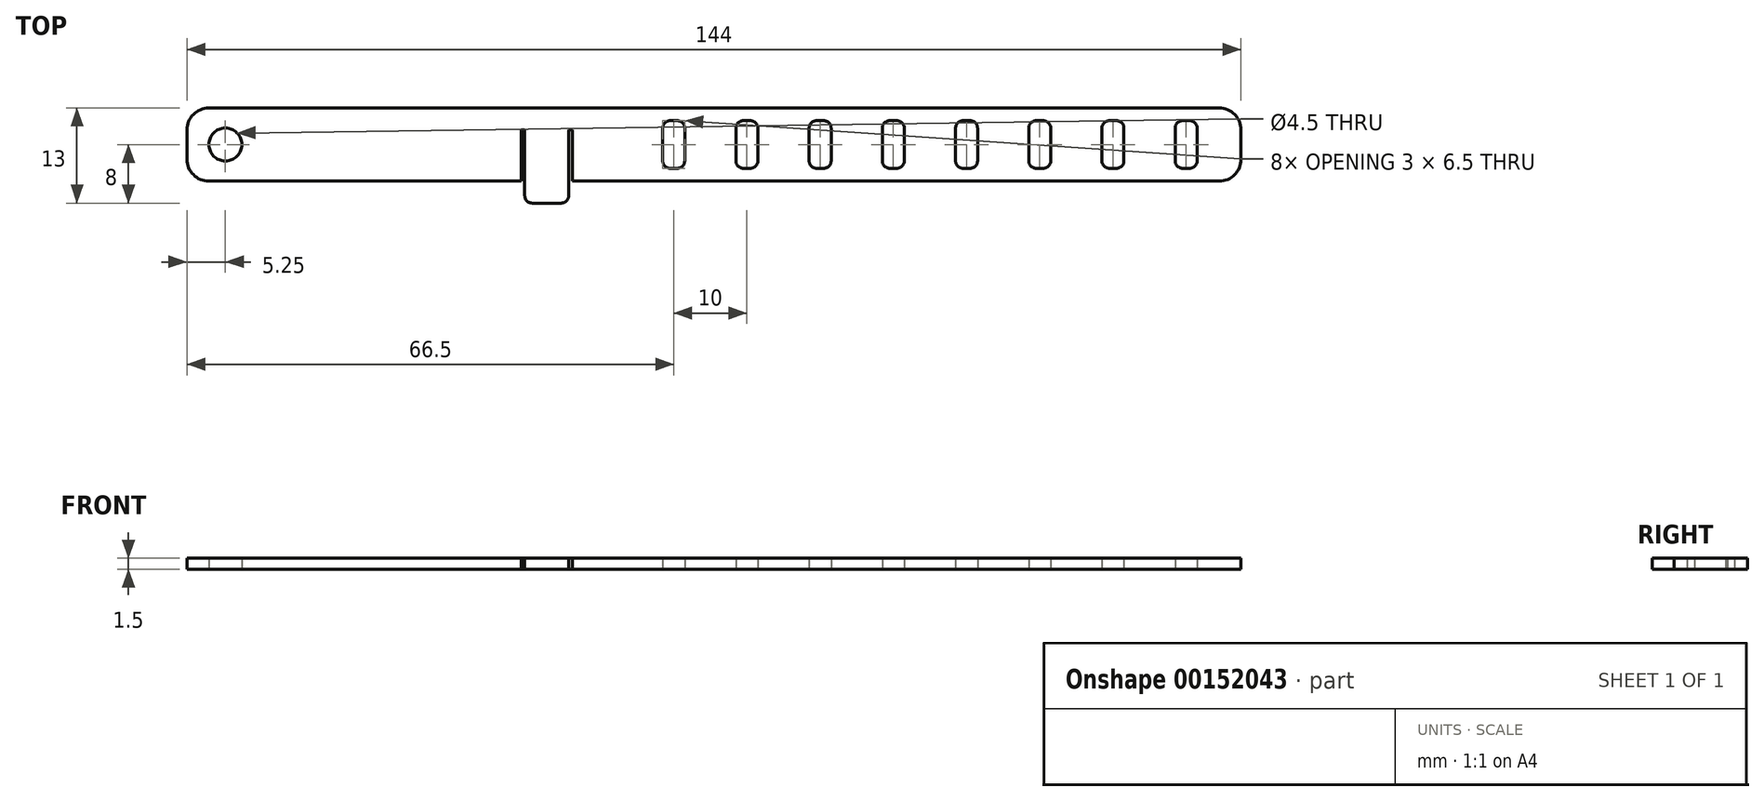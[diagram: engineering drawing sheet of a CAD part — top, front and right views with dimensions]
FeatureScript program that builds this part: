
annotation { "Feature Type Name" : "Feature", "Feature Type Description" : "" }
export const myFeature = defineFeature(function(context is Context, id is Id, definition is map)
    precondition{}
    {
        {
            var Q0;
            Q0=qCreatedBy(makeId("Top.planeOp"),FACE);
            var sketch = newSketch(context, id + "F0", { "sketchPlane" : qUnion([Q0])});
            skLineSegment(sketch, "E0.bottom", {"start": v(69, -5) * mm, "end": v(-19.85, -5) * mm});
            skLineSegment(sketch, "E0.top", {"start": v(69, 5) * mm, "end": v(-69, 5) * mm});
            skLineSegment(sketch, "E0.left", {"start": v(72, -2) * mm, "end": v(72, 2) * mm});
            skLineSegment(sketch, "E0.right", {"start": v(-72, -2) * mm, "end": v(-72, 2) * mm});
            skPoint(sketch, "E0.middle", {"position": v(0, 0) * mm});
            skPoint(sketch, "E1.visualSharp", {"position": v(-72, 5) * mm});
            skArc(sketch, "E1.filletArc", {"start": v(-69, 5) * mm, "mid": v(-71.12, 4.12) * mm, "end": v(-72, 2) * mm});
            skPoint(sketch, "E2.visualSharp", {"position": v(-72, -5) * mm});
            skArc(sketch, "E2.filletArc", {"start": v(-72, -2) * mm, "mid": v(-71.12, -4.12) * mm, "end": v(-69, -5) * mm});
            skPoint(sketch, "E3.visualSharp", {"position": v(72, 5) * mm});
            skArc(sketch, "E3.filletArc", {"start": v(72, 2) * mm, "mid": v(71.12, 4.12) * mm, "end": v(69, 5) * mm});
            skPoint(sketch, "E4.visualSharp", {"position": v(72, -5) * mm});
            skArc(sketch, "E4.filletArc", {"start": v(69, -5) * mm, "mid": v(71.12, -4.12) * mm, "end": v(72, -2) * mm});
            skLineSegment(sketch, "E5.bottom", {"start": v(-5, -3.25) * mm, "end": v(-6, -3.25) * mm});
            skLineSegment(sketch, "E5.top", {"start": v(-5, 3.25) * mm, "end": v(-6, 3.25) * mm});
            skLineSegment(sketch, "E5.left", {"start": v(-4, -2.25) * mm, "end": v(-4, 2.25) * mm});
            skLineSegment(sketch, "E5.right", {"start": v(-7, -2.25) * mm, "end": v(-7, 2.25) * mm});
            skPoint(sketch, "E5.middle", {"position": v(-5.5, 0) * mm});
            skPoint(sketch, "E6.visualSharp", {"position": v(-7, 3.25) * mm});
            skArc(sketch, "E6.filletArc", {"start": v(-6, 3.25) * mm, "mid": v(-6.7, 2.96) * mm, "end": v(-7, 2.25) * mm});
            skPoint(sketch, "E7.visualSharp", {"position": v(-4, 3.25) * mm});
            skArc(sketch, "E7.filletArc", {"start": v(-4, 2.25) * mm, "mid": v(-4.3, 2.96) * mm, "end": v(-5, 3.25) * mm});
            skPoint(sketch, "E8.visualSharp", {"position": v(-4, -3.25) * mm});
            skArc(sketch, "E8.filletArc", {"start": v(-5, -3.25) * mm, "mid": v(-4.3, -2.96) * mm, "end": v(-4, -2.25) * mm});
            skPoint(sketch, "E9.visualSharp", {"position": v(-7, -3.25) * mm});
            skArc(sketch, "E9.filletArc", {"start": v(-7, -2.25) * mm, "mid": v(-6.7, -2.96) * mm, "end": v(-6, -3.25) * mm});
            skLineSegment(sketch, "E10.1.0.0", {"start": v(3, -2.25) * mm, "end": v(3, 2.25) * mm});
            skArc(sketch, "E10.1.0.1", {"start": v(4, 3.25) * mm, "mid": v(3.3, 2.96) * mm, "end": v(3, 2.25) * mm});
            skLineSegment(sketch, "E10.1.0.2", {"start": v(5, 3.25) * mm, "end": v(4, 3.25) * mm});
            skArc(sketch, "E10.1.0.3", {"start": v(6, 2.25) * mm, "mid": v(5.7, 2.96) * mm, "end": v(5, 3.25) * mm});
            skLineSegment(sketch, "E10.1.0.4", {"start": v(6, -2.25) * mm, "end": v(6, 2.25) * mm});
            skArc(sketch, "E10.1.0.5", {"start": v(5, -3.25) * mm, "mid": v(5.7, -2.96) * mm, "end": v(6, -2.25) * mm});
            skLineSegment(sketch, "E10.1.0.6", {"start": v(5, -3.25) * mm, "end": v(4, -3.25) * mm});
            skArc(sketch, "E10.1.0.7", {"start": v(3, -2.25) * mm, "mid": v(3.3, -2.96) * mm, "end": v(4, -3.25) * mm});
            skLineSegment(sketch, "E10.2.0.0", {"start": v(13, -2.25) * mm, "end": v(13, 2.25) * mm});
            skArc(sketch, "E10.2.0.1", {"start": v(14, 3.25) * mm, "mid": v(13.3, 2.96) * mm, "end": v(13, 2.25) * mm});
            skLineSegment(sketch, "E10.2.0.2", {"start": v(15, 3.25) * mm, "end": v(14, 3.25) * mm});
            skArc(sketch, "E10.2.0.3", {"start": v(16, 2.25) * mm, "mid": v(15.7, 2.96) * mm, "end": v(15, 3.25) * mm});
            skLineSegment(sketch, "E10.2.0.4", {"start": v(16, -2.25) * mm, "end": v(16, 2.25) * mm});
            skArc(sketch, "E10.2.0.5", {"start": v(15, -3.25) * mm, "mid": v(15.7, -2.96) * mm, "end": v(16, -2.25) * mm});
            skLineSegment(sketch, "E10.2.0.6", {"start": v(15, -3.25) * mm, "end": v(14, -3.25) * mm});
            skArc(sketch, "E10.2.0.7", {"start": v(13, -2.25) * mm, "mid": v(13.3, -2.96) * mm, "end": v(14, -3.25) * mm});
            skLineSegment(sketch, "E10.3.0.0", {"start": v(23, -2.25) * mm, "end": v(23, 2.25) * mm});
            skArc(sketch, "E10.3.0.1", {"start": v(24, 3.25) * mm, "mid": v(23.3, 2.96) * mm, "end": v(23, 2.25) * mm});
            skLineSegment(sketch, "E10.3.0.2", {"start": v(25, 3.25) * mm, "end": v(24, 3.25) * mm});
            skArc(sketch, "E10.3.0.3", {"start": v(26, 2.25) * mm, "mid": v(25.7, 2.96) * mm, "end": v(25, 3.25) * mm});
            skLineSegment(sketch, "E10.3.0.4", {"start": v(26, -2.25) * mm, "end": v(26, 2.25) * mm});
            skArc(sketch, "E10.3.0.5", {"start": v(25, -3.25) * mm, "mid": v(25.7, -2.96) * mm, "end": v(26, -2.25) * mm});
            skLineSegment(sketch, "E10.3.0.6", {"start": v(25, -3.25) * mm, "end": v(24, -3.25) * mm});
            skArc(sketch, "E10.3.0.7", {"start": v(23, -2.25) * mm, "mid": v(23.3, -2.96) * mm, "end": v(24, -3.25) * mm});
            skLineSegment(sketch, "E10.4.0.0", {"start": v(33, -2.25) * mm, "end": v(33, 2.25) * mm});
            skArc(sketch, "E10.4.0.1", {"start": v(34, 3.25) * mm, "mid": v(33.3, 2.96) * mm, "end": v(33, 2.25) * mm});
            skLineSegment(sketch, "E10.4.0.2", {"start": v(35, 3.25) * mm, "end": v(34, 3.25) * mm});
            skArc(sketch, "E10.4.0.3", {"start": v(36, 2.25) * mm, "mid": v(35.7, 2.96) * mm, "end": v(35, 3.25) * mm});
            skLineSegment(sketch, "E10.4.0.4", {"start": v(36, -2.25) * mm, "end": v(36, 2.25) * mm});
            skArc(sketch, "E10.4.0.5", {"start": v(35, -3.25) * mm, "mid": v(35.7, -2.96) * mm, "end": v(36, -2.25) * mm});
            skLineSegment(sketch, "E10.4.0.6", {"start": v(35, -3.25) * mm, "end": v(34, -3.25) * mm});
            skArc(sketch, "E10.4.0.7", {"start": v(33, -2.25) * mm, "mid": v(33.3, -2.96) * mm, "end": v(34, -3.25) * mm});
            skLineSegment(sketch, "E10.5.0.0", {"start": v(43, -2.25) * mm, "end": v(43, 2.25) * mm});
            skArc(sketch, "E10.5.0.1", {"start": v(44, 3.25) * mm, "mid": v(43.3, 2.96) * mm, "end": v(43, 2.25) * mm});
            skLineSegment(sketch, "E10.5.0.2", {"start": v(45, 3.25) * mm, "end": v(44, 3.25) * mm});
            skArc(sketch, "E10.5.0.3", {"start": v(46, 2.25) * mm, "mid": v(45.7, 2.96) * mm, "end": v(45, 3.25) * mm});
            skLineSegment(sketch, "E10.5.0.4", {"start": v(46, -2.25) * mm, "end": v(46, 2.25) * mm});
            skArc(sketch, "E10.5.0.5", {"start": v(45, -3.25) * mm, "mid": v(45.7, -2.96) * mm, "end": v(46, -2.25) * mm});
            skLineSegment(sketch, "E10.5.0.6", {"start": v(45, -3.25) * mm, "end": v(44, -3.25) * mm});
            skArc(sketch, "E10.5.0.7", {"start": v(43, -2.25) * mm, "mid": v(43.3, -2.96) * mm, "end": v(44, -3.25) * mm});
            skLineSegment(sketch, "E10.6.0.0", {"start": v(53, -2.25) * mm, "end": v(53, 2.25) * mm});
            skArc(sketch, "E10.6.0.1", {"start": v(54, 3.25) * mm, "mid": v(53.3, 2.96) * mm, "end": v(53, 2.25) * mm});
            skLineSegment(sketch, "E10.6.0.2", {"start": v(55, 3.25) * mm, "end": v(54, 3.25) * mm});
            skArc(sketch, "E10.6.0.3", {"start": v(56, 2.25) * mm, "mid": v(55.7, 2.96) * mm, "end": v(55, 3.25) * mm});
            skLineSegment(sketch, "E10.6.0.4", {"start": v(56, -2.25) * mm, "end": v(56, 2.25) * mm});
            skArc(sketch, "E10.6.0.5", {"start": v(55, -3.25) * mm, "mid": v(55.7, -2.96) * mm, "end": v(56, -2.25) * mm});
            skLineSegment(sketch, "E10.6.0.6", {"start": v(55, -3.25) * mm, "end": v(54, -3.25) * mm});
            skArc(sketch, "E10.6.0.7", {"start": v(53, -2.25) * mm, "mid": v(53.3, -2.96) * mm, "end": v(54, -3.25) * mm});
            skLineSegment(sketch, "E10.7.0.0", {"start": v(63, -2.25) * mm, "end": v(63, 2.25) * mm});
            skArc(sketch, "E10.7.0.1", {"start": v(64, 3.25) * mm, "mid": v(63.3, 2.96) * mm, "end": v(63, 2.25) * mm});
            skLineSegment(sketch, "E10.7.0.2", {"start": v(65, 3.25) * mm, "end": v(64, 3.25) * mm});
            skArc(sketch, "E10.7.0.3", {"start": v(66, 2.25) * mm, "mid": v(65.7, 2.96) * mm, "end": v(65, 3.25) * mm});
            skLineSegment(sketch, "E10.7.0.4", {"start": v(66, -2.25) * mm, "end": v(66, 2.25) * mm});
            skArc(sketch, "E10.7.0.5", {"start": v(65, -3.25) * mm, "mid": v(65.7, -2.96) * mm, "end": v(66, -2.25) * mm});
            skLineSegment(sketch, "E10.7.0.6", {"start": v(65, -3.25) * mm, "end": v(64, -3.25) * mm});
            skArc(sketch, "E10.7.0.7", {"start": v(63, -2.25) * mm, "mid": v(63.3, -2.96) * mm, "end": v(64, -3.25) * mm});
            skLineSegment(sketch, "E10.direction1", {"start": v(-7, -2.25) * mm, "end": v(3, -2.25) * mm, "construction": true});
            skCircle(sketch, "E11", {"center": v(-66.75, 0) * mm, "radius": 2.25 * mm});
            skPoint(sketch, "E12.middle", {"position": v(-22, 2) * mm});
            skPoint(sketch, "E13.middle", {"position": v(-22, -2) * mm});
            skPoint(sketch, "E12.right.end.orphan", {"position": v(-27, 3) * mm});
            skPoint(sketch, "E12.right.start.orphan", {"position": v(-27, 1) * mm});
            skPoint(sketch, "E12.left.end.orphan", {"position": v(-17, 3) * mm});
            skPoint(sketch, "E12.left.start.orphan", {"position": v(-17, 1) * mm});
            skLineSegment(sketch, "E14.left", {"start": v(-27, -1) * mm, "end": v(-27, -1) * mm});
            skLineSegment(sketch, "E14.right", {"start": v(-17, -1) * mm, "end": v(-17, -1) * mm});
            skPoint(sketch, "E15.top.end.orphan", {"position": v(-17, -12.72) * mm});
            skPoint(sketch, "E16.trimOffspring.start.orphan", {"position": v(-17, -3) * mm});
            skLineSegment(sketch, "E17.bottom", {"start": v(-25.85, 2) * mm, "end": v(-19.85, 2) * mm});
            skLineSegment(sketch, "E17.top", {"start": v(-25.85, -8) * mm, "end": v(-19.85, -8) * mm});
            skLineSegment(sketch, "E17.left", {"start": v(-25.85, 2) * mm, "end": v(-25.85, -8) * mm});
            skLineSegment(sketch, "E17.right", {"start": v(-19.85, 2) * mm, "end": v(-19.85, -8) * mm});
            skPoint(sketch, "E13.right.start.orphan", {"position": v(-27, -3) * mm});
            skLineSegment(sketch, "E18", {"start": v(-26.35, -5) * mm, "end": v(-26.35, 2) * mm});
            skLineSegment(sketch, "E19", {"start": v(-26.35, 2) * mm, "end": v(-19.35, 2) * mm});
            skLineSegment(sketch, "E20", {"start": v(-19.35, 2) * mm, "end": v(-19.35, -5) * mm});
            skLineSegment(sketch, "E21.trimOffspring", {"start": v(-25.85, -5) * mm, "end": v(-69, -5) * mm});
            skSolve(sketch);
        }
        {
            var Q0;
            Q0=makeQuery(id+"F0.imprint","IMPRINT",FACE,{"disambiguationData":[TD([[makeQuery(id+"F0.imprint","IMPRINT",EDGE,{"derivedFrom":sQuery(id+"F0.wireOp",EDGE,"E0.top")}),1.0]])]});
            var Q1;
            {var subQ5=sQuery(id+"F0.wireOp",EDGE,"E17.bottom");Q1=makeQuery(id+"F0.imprint","IMPRINT",FACE,{"disambiguationData":[TD([[makeQuery(id+"F0.imprint","IMPRINT",EDGE,{"derivedFrom":subQ5}),-1.0]])]});}
            var Q2;
            {var subQ5=sQuery(id+"F0.wireOp",EDGE,"E17.top");Q2=makeQuery(id+"F0.imprint","IMPRINT",FACE,{"disambiguationData":[TD([[makeQuery(id+"F0.imprint","IMPRINT",EDGE,{"derivedFrom":subQ5}),1.0]])]});}
            extrude(context, id + "F1", {"entities" : qUnion([Q0, Q1, Q2]), "depth" : 1.5 * mm});
        }
        {
            var Q0;
            Q0=makeQuery(id+"F1.opExtrude","SWEPT_EDGE",EDGE,{"disambiguationData":[OSD([sQuery(id+"F0.wireOp",EDGE,"E17.top"),sQuery(id+"F0.wireOp",EDGE,"E17.left")])]});
            var Q1;
            Q1=makeQuery(id+"F1.opExtrude","SWEPT_EDGE",EDGE,{"disambiguationData":[OSD([sQuery(id+"F0.wireOp",EDGE,"E17.top"),sQuery(id+"F0.wireOp",EDGE,"E17.right")])]});
            fillet(context, id + "F2", {"entities" : qUnion([Q0, Q1]), "radius" : 1 * mm, "tangentPropagation" : true, "allowEdgeOverflow" : false});
        }
    });
